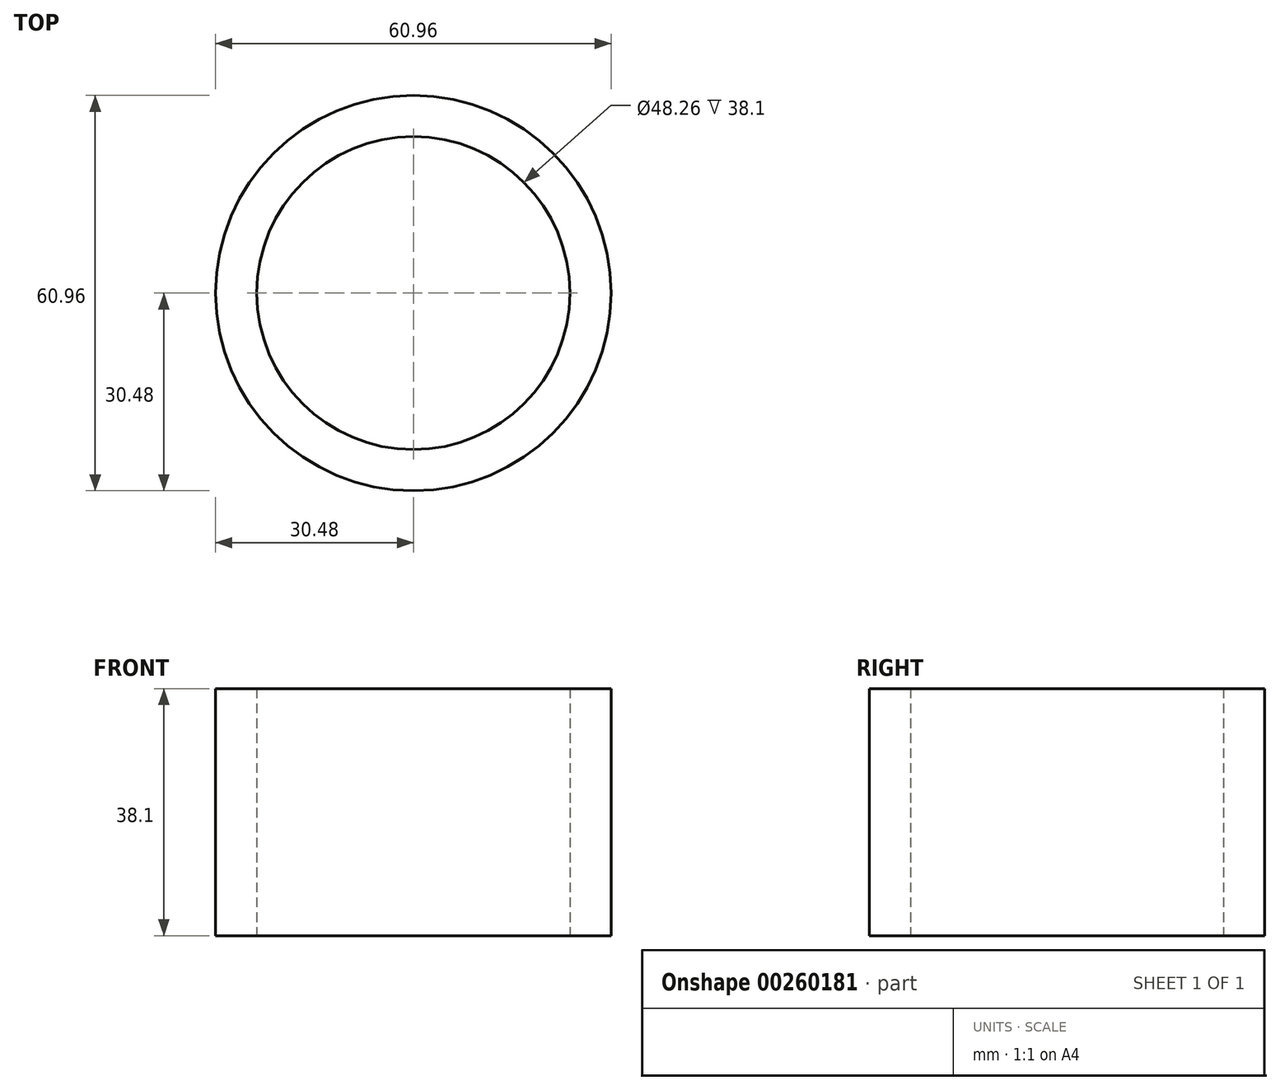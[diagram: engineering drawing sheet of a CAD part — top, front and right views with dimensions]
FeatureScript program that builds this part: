
annotation { "Feature Type Name" : "Feature", "Feature Type Description" : "" }
export const myFeature = defineFeature(function(context is Context, id is Id, definition is map)
    precondition{}
    {
        {
            var Q0;
            Q0=qCreatedBy(makeId("Top.planeOp"),FACE);
            var sketch = newSketch(context, id + "F0", { "sketchPlane" : qUnion([Q0])});
            skCircle(sketch, "E0", {"center": v(0, 0) * mm, "radius": 30.48 * mm});
            skCircle(sketch, "E1.0", {"center": v(0, 0) * mm, "radius": 24.13 * mm});
            skSolve(sketch);
        }
        {
            var Q0;
            Q0 = qSketchRegion(id + "F0", true);
            extrude(context, id + "F1", {"entities" : qUnion([Q0]), "depth" : 38.1 * mm});
        }
    });
